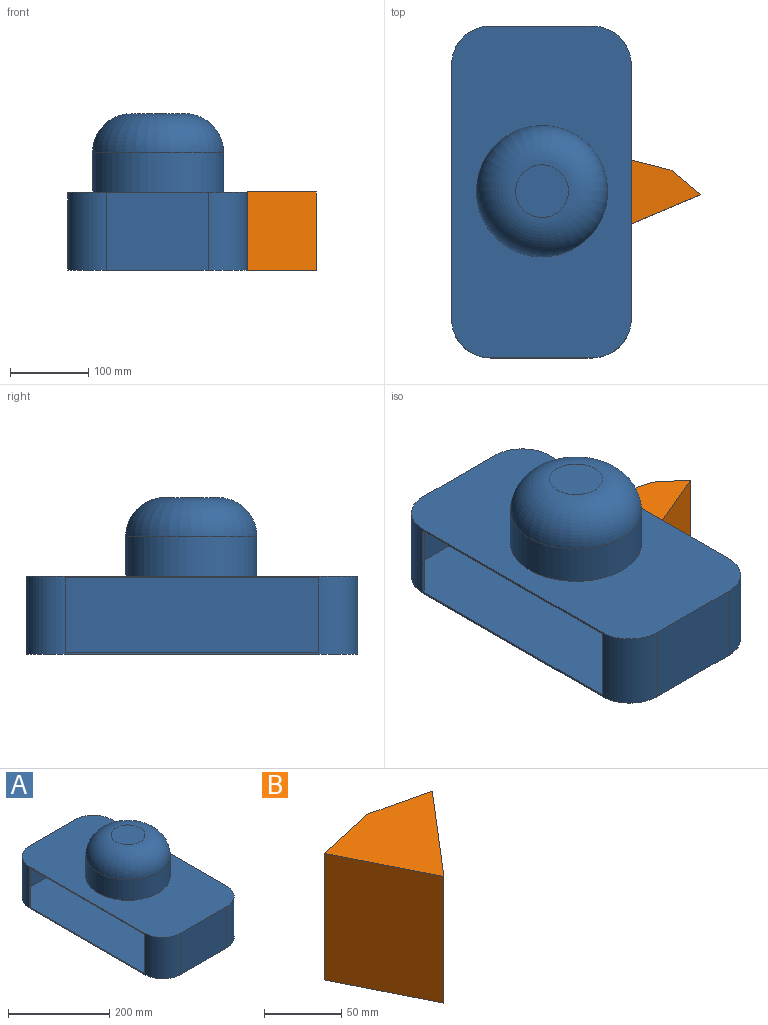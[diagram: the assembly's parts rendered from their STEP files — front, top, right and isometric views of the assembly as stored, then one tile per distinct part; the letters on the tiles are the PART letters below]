
ASSEMBLY  parts=2 mates=1
PART A: 28 faces, bbox 229.1x423x200 mm
  f0: plane 322.97x2.5mm, normal (-1,0,0), area 807.4mm2, adj f2,f4,f10,f24
  f1: plane 129.08x100mm, normal (0,1,0), area 12907.6mm2, adj f2,f8,f9,f10
  f2: cylinder r=50mm len=100mm, axis (0,0,-1), area 7854mm2, adj f0,f1,f3,f9,f10,f14
  f3: plane 322.97x2.5mm, normal (-1,0,0), area 807.4mm2, adj f2,f4,f9,f23
  f4: cylinder r=50mm len=100mm, axis (0,0,-1), area 7854mm2, adj f0,f3,f5,f9,f10,f15
  f5: plane 129.08x100mm, normal (0,-1,0), area 12907.6mm2, adj f4,f6,f9,f10
  f6: cylinder r=50mm len=100mm, axis (0,0,-1), area 7854mm2, adj f5,f7,f9,f10
  f7: plane 322.97x100mm, normal (1,0,0), area 32296.6mm2, adj f6,f8,f9,f10
  f8: cylinder r=50mm len=100mm, axis (0,0,-1), area 7854mm2, adj f1,f7,f9,f10
  f9: plane 422.97x229.08mm, normal (0,0,1), area 72771mm2, adj f1,f2,f3,f4,f5,f6,f7,f8
  f10: plane 422.97x229.08mm, normal (0,0,-1), area 94745.5mm2, adj f0,f1,f2,f4,f5,f6,f7,f8
  f11: cylinder r=83.63mm len=167.27mm, axis (0,0,-1), area 26274.5mm2, adj f9,f13
  f12: plane 67.27x67.27mm, normal (0,0,1), area 3554mm2, adj f13
  f13: torus R=33.63mm, axis (0,0,1), area 32305.8mm2, adj f11,f12
  f14: plane 95x2.5mm, normal (0,-1,0), area 237.5mm2, adj f2,f17,f23,f24
  f15: plane 95x2.5mm, normal (0,1,0), area 237.5mm2, adj f4,f18,f23,f24
  f16: plane 129.08x95mm, normal (0,-1,0), area 12262.2mm2, adj f17,f22,f23,f24
  f17: cylinder r=47.5mm len=95mm, axis (0,0,-1), area 7088.2mm2, adj f14,f16,f23,f24
  f18: cylinder r=47.5mm len=95mm, axis (0,0,-1), area 7088.2mm2, adj f15,f19,f23,f24
  f19: plane 129.08x95mm, normal (0,1,0), area 12262.2mm2, adj f18,f20,f23,f24
  f20: cylinder r=47.5mm len=95mm, axis (0,0,-1), area 7088.2mm2, adj f19,f21,f23,f24
  f21: plane 322.97x95mm, normal (-1,0,0), area 30681.8mm2, adj f20,f22,f23,f24
  f22: cylinder r=47.5mm len=95mm, axis (0,0,-1), area 7088.2mm2, adj f16,f21,f23,f24
  f23: plane 417.97x226.58mm, normal (0,0,-1), area 71846.6mm2, adj f3,f14,f15,f16,f17,f18,f19,f20
  f24: plane 417.97x226.58mm, normal (0,0,1), area 92527mm2, adj f0,f14,f15,f16,f17,f18,f19,f20
  f25: cylinder r=81.13mm len=162.27mm, axis (0,0,-1), area 26763.5mm2, adj f23,f27
  f26: plane 67.27x67.27mm, normal (0,0,-1), area 3554mm2, adj f27
  f27: torus R=33.63mm, axis (0,0,1), area 29944.4mm2, adj f25,f26
PART B: 6 faces, bbox 98.7x84x100 mm
  f0: plane 100x72.84mm, normal (-0.89,-0.45,0), area 8144.3mm2, adj f1,f3,f4,f5
  f1: plane 100x72.84mm, normal (0.76,-0.65,0), area 9582mm2, adj f0,f2,f4,f5
  f2: plane 100x47.59mm, normal (0.23,0.97,0), area 4887.6mm2, adj f1,f3,f4,f5
  f3: plane 100x51.1mm, normal (-0.21,0.98,0), area 5230mm2, adj f0,f2,f4,f5
  f4: plane 98.69x83.97mm, normal (0,0,1), area 4143.5mm2, adj f0,f1,f2,f3
  f5: plane 98.69x83.97mm, normal (0,0,-1), area 4143.5mm2, adj f0,f1,f2,f3
PLACE A t=(-211.82,46.34,-33.3)mm
PLACE B rot(axis=(0,0,-1),26.6deg) t=(269.79,106.37,-33.3)mm
MATE fastened B.f0 <-> A.f7  axis (-1,0,0) through (237.2,81.95,-33.3)mm
